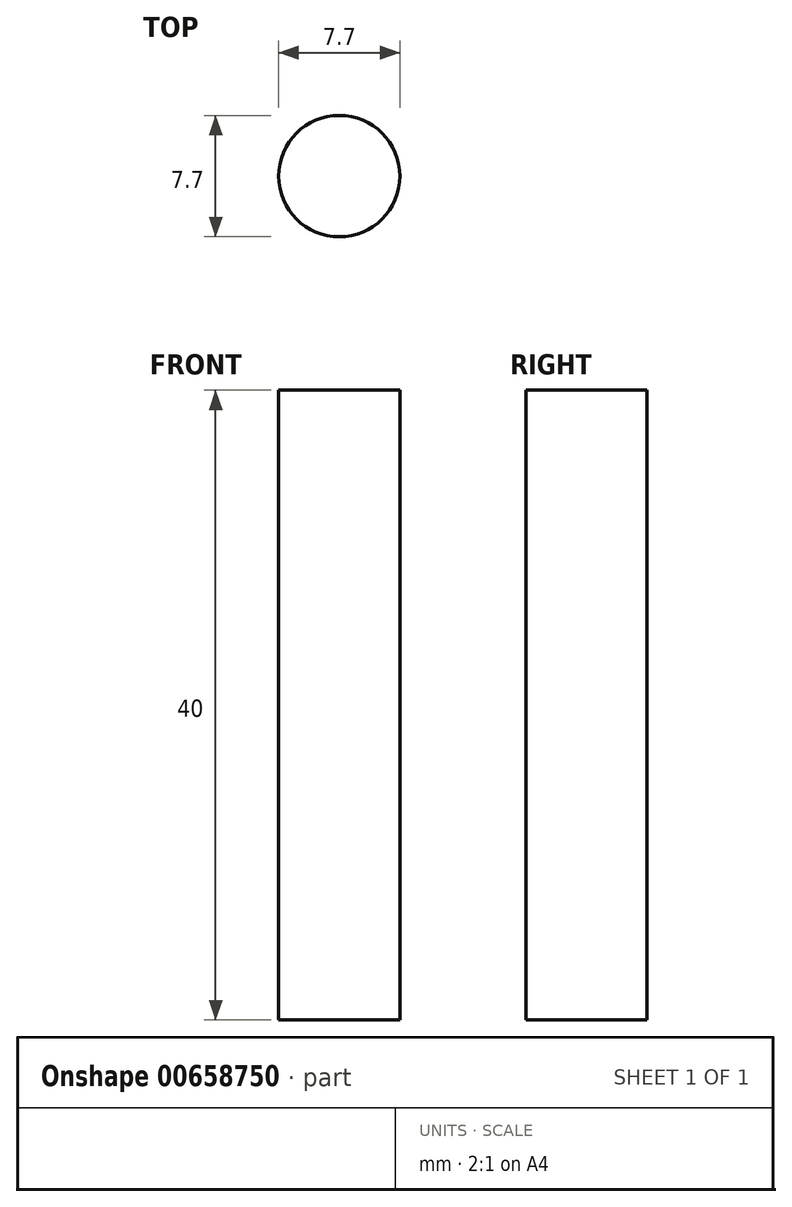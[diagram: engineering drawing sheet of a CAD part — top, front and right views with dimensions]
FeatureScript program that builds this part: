
annotation { "Feature Type Name" : "Feature", "Feature Type Description" : "" }
export const myFeature = defineFeature(function(context is Context, id is Id, definition is map)
    precondition{}
    {
        {
            var Q0;
            Q0=qCreatedBy(makeId("Top.planeOp"),FACE);
            var sketch = newSketch(context, id + "F0", { "sketchPlane" : qUnion([Q0])});
            skCircle(sketch, "E0", {"center": v(0, 0) * mm, "radius": 3.85 * mm});
            skCircle(sketch, "E1", {"center": v(0, -18.75) * mm, "radius": 3.85 * mm});
            skCircle(sketch, "E2", {"center": v(-22.47, -18.75) * mm, "radius": 3.85 * mm});
            skCircle(sketch, "E3", {"center": v(-22.47, 0) * mm, "radius": 3.85 * mm});
            skSolve(sketch);
        }
        {
            var Q0;
            Q0 = qSketchRegion(id + "F0", true);
            extrude(context, id + "F1", {"entities" : qUnion([Q0]), "depth" : 25 * mm, "offsetDistance" : 25 * mm});
        }
        {
            var Q0;
            Q0=makeQuery(id+"F1.opExtrude","CAP_FACE",FACE,{"disambiguationData":[OSD([sQuery(id+"F0.wireOp",EDGE,"E2")])],"isStart":false});
            extrude(context, id + "F2", {"entities" : qUnion([Q0]), "operationType" : NewBodyOperationType.ADD, "depth" : 10 * mm, "offsetDistance" : 25 * mm});
        }
        {
            var Q0;
            Q0=makeQuery(id+"F1.opExtrude","CAP_FACE",FACE,{"disambiguationData":[OSD([sQuery(id+"F0.wireOp",EDGE,"E3")])],"isStart":false});
            extrude(context, id + "F3", {"entities" : qUnion([Q0]), "operationType" : NewBodyOperationType.ADD, "depth" : 15 * mm, "offsetDistance" : 25 * mm});
        }
        {
            var Q0;
            Q0=makeQuery(id+"F1.opExtrude","SWEPT_BODY",BODY,{"disambiguationData":[OSD([sQuery(id+"F0.wireOp",EDGE,"E2")])]});
            var Q1;
            Q1=makeQuery(id+"F1.opExtrude","SWEPT_BODY",BODY,{"disambiguationData":[OSD([sQuery(id+"F0.wireOp",EDGE,"E1")])]});
            var Q2;
            Q2=makeQuery(id+"F1.opExtrude","SWEPT_BODY",BODY,{"disambiguationData":[OSD([sQuery(id+"F0.wireOp",EDGE,"E0")])]});
            deleteBodies(context, id + "F4", {"entities" : qUnion([Q0, Q1, Q2])});
        }
    });
